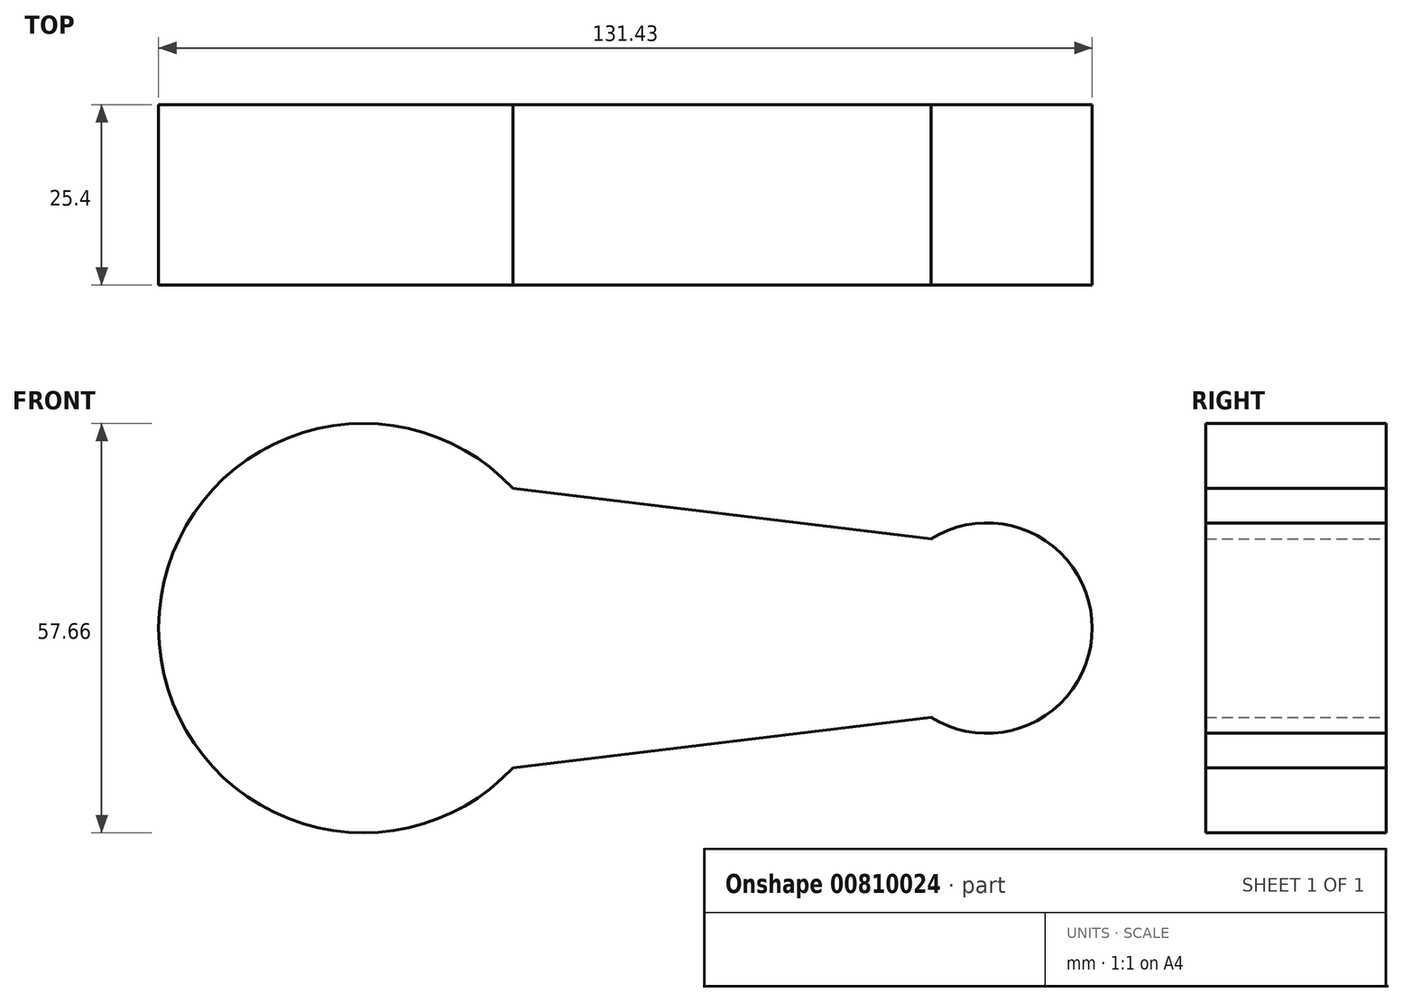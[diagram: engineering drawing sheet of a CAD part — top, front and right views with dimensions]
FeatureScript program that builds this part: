
annotation { "Feature Type Name" : "Feature", "Feature Type Description" : "" }
export const myFeature = defineFeature(function(context is Context, id is Id, definition is map)
    precondition{}
    {
        {
            var Q0;
            Q0=qCreatedBy(makeId("Front.planeOp"),FACE);
            var sketch = newSketch(context, id + "F0", { "sketchPlane" : qUnion([Q0])});
            skCircle(sketch, "E0", {"center": v(-39.3, 0) * mm, "radius": 28.83 * mm});
            skCircle(sketch, "E1", {"center": v(48.48, 0) * mm, "radius": 14.82 * mm});
            skLineSegment(sketch, "E2", {"start": v(-18.24, 19.67) * mm, "end": v(40.6, 12.55) * mm});
            skLineSegment(sketch, "E3.MirrorCS", {"start": v(-18.24, -19.67) * mm, "end": v(40.6, -12.55) * mm});
            skSolve(sketch);
        }
        {
            var Q0;
            Q0 = qSketchRegion(id + "F0", true);
            extrude(context, id + "F1", {"entities" : qUnion([Q0]), "endBound" : BoundingType.SYMMETRIC, "depth" : 25.4 * mm, "offsetDistance" : 25.4 * mm});
        }
    });
